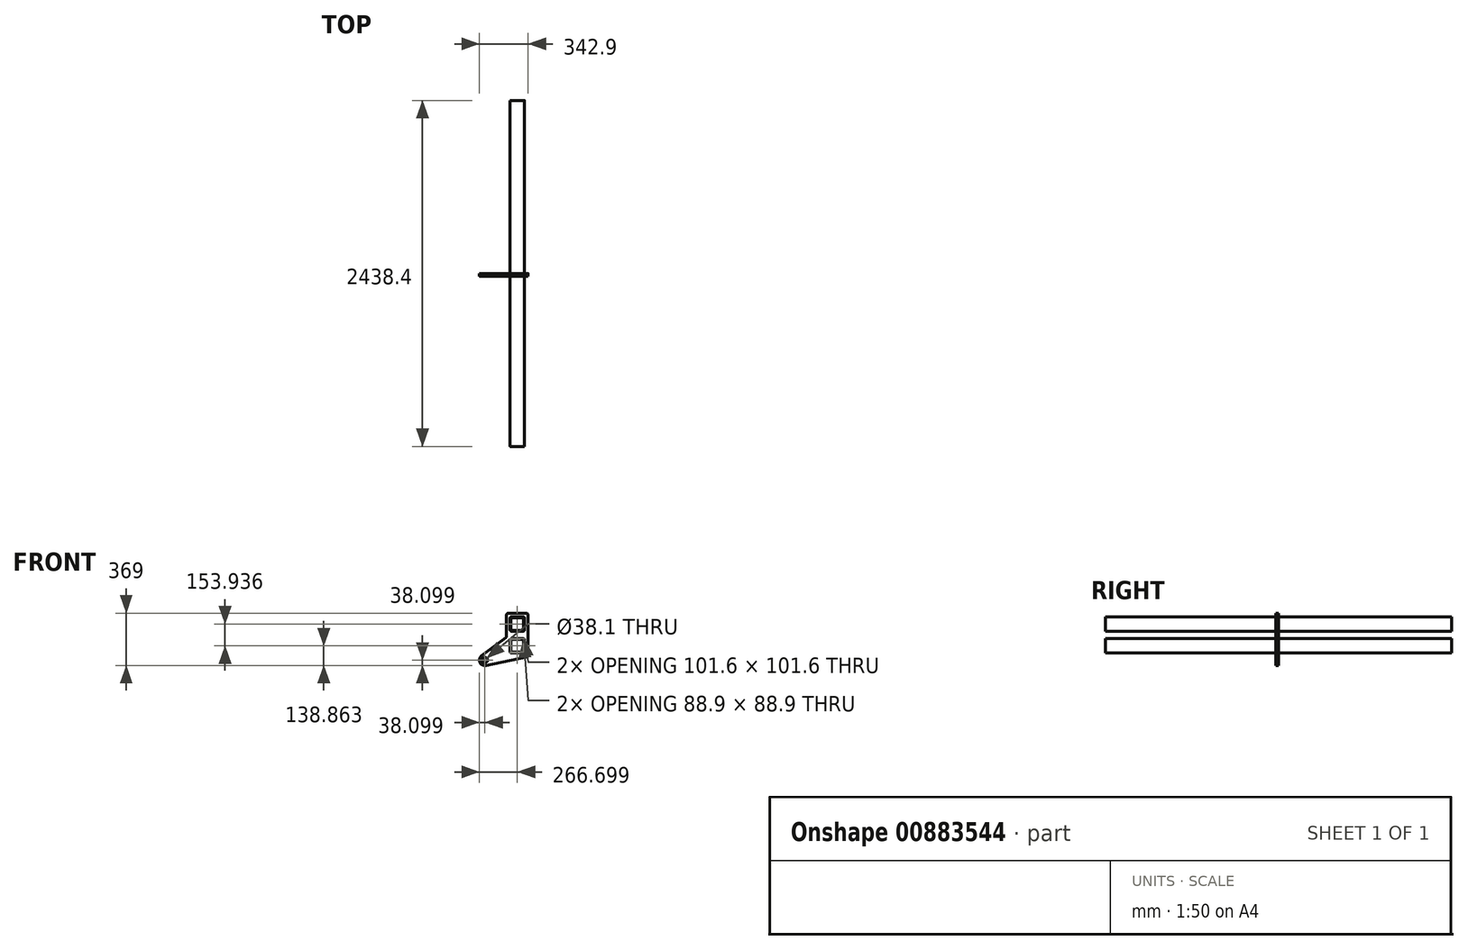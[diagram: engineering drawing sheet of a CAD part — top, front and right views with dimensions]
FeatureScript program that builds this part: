
annotation { "Feature Type Name" : "Feature", "Feature Type Description" : "" }
export const myFeature = defineFeature(function(context is Context, id is Id, definition is map)
    precondition{}
    {
        {
            var Q0;
            Q0=qCreatedBy(makeId("Front.planeOp"),FACE);
            var sketch = newSketch(context, id + "F0", { "sketchPlane" : qUnion([Q0])});
            skLineSegment(sketch, "E0.bottom", {"start": v(-15.4, 19.87) * mm, "end": v(66.9, 19.87) * mm});
            skLineSegment(sketch, "E0.top", {"start": v(-15.4, -81.73) * mm, "end": v(66.9, -81.73) * mm});
            skLineSegment(sketch, "E0.left", {"start": v(-25.05, 10.22) * mm, "end": v(-25.05, -72.07) * mm});
            skLineSegment(sketch, "E0.right", {"start": v(76.55, 10.22) * mm, "end": v(76.55, -72.07) * mm});
            skLineSegment(sketch, "E1.bottom", {"start": v(-9.05, 13.52) * mm, "end": v(60.55, 13.52) * mm});
            skLineSegment(sketch, "E1.top", {"start": v(-9.05, -75.38) * mm, "end": v(60.55, -75.38) * mm});
            skLineSegment(sketch, "E1.left", {"start": v(-18.7, 3.87) * mm, "end": v(-18.7, -65.72) * mm});
            skLineSegment(sketch, "E1.right", {"start": v(70.2, 3.87) * mm, "end": v(70.2, -65.72) * mm});
            skLineSegment(sketch, "E2.bottom", {"start": v(-15.4, 173.8) * mm, "end": v(66.9, 173.8) * mm});
            skLineSegment(sketch, "E2.top", {"start": v(-15.4, 72.2) * mm, "end": v(66.9, 72.2) * mm});
            skLineSegment(sketch, "E2.left", {"start": v(-25.05, 164.16) * mm, "end": v(-25.05, 81.86) * mm});
            skLineSegment(sketch, "E2.right", {"start": v(76.55, 164.16) * mm, "end": v(76.55, 81.86) * mm});
            skLineSegment(sketch, "E3.bottom", {"start": v(-9.05, 167.46) * mm, "end": v(60.55, 167.46) * mm});
            skLineSegment(sketch, "E3.top", {"start": v(-9.05, 78.56) * mm, "end": v(60.55, 78.56) * mm});
            skLineSegment(sketch, "E3.left", {"start": v(-18.7, 157.8) * mm, "end": v(-18.7, 88.21) * mm});
            skLineSegment(sketch, "E3.right", {"start": v(70.2, 157.8) * mm, "end": v(70.2, 88.21) * mm});
            skLineSegment(sketch, "E4.bottom", {"start": v(-37.75, 199.2) * mm, "end": v(89.25, 199.2) * mm});
            skLineSegment(sketch, "E4.left", {"start": v(-50.45, 186.5) * mm, "end": v(-50.45, 36.8) * mm});
            skLineSegment(sketch, "E4.right", {"start": v(101.95, 186.5) * mm, "end": v(101.95, -96.8) * mm});
            skArc(sketch, "E5", {"start": v(-225.74, -101.23) * mm, "mid": v(-237.56, -147.4) * mm, "end": v(-195.08, -169) * mm});
            skCircle(sketch, "E6", {"center": v(-202.85, -131.7) * mm, "radius": 19.05 * mm});
            skPoint(sketch, "E7.visualSharp", {"position": v(-18.7, 167.46) * mm});
            skArc(sketch, "E7.filletArc", {"start": v(-9.05, 167.46) * mm, "mid": v(-15.87, 164.63) * mm, "end": v(-18.7, 157.8) * mm});
            skPoint(sketch, "E8.visualSharp", {"position": v(70.2, 167.46) * mm});
            skArc(sketch, "E8.filletArc", {"start": v(70.2, 157.8) * mm, "mid": v(67.37, 164.63) * mm, "end": v(60.55, 167.46) * mm});
            skPoint(sketch, "E9.visualSharp", {"position": v(70.2, 78.56) * mm});
            skArc(sketch, "E9.filletArc", {"start": v(60.55, 78.56) * mm, "mid": v(67.37, 81.39) * mm, "end": v(70.2, 88.21) * mm});
            skPoint(sketch, "E10.visualSharp", {"position": v(-18.7, 78.56) * mm});
            skArc(sketch, "E10.filletArc", {"start": v(-18.7, 88.21) * mm, "mid": v(-15.87, 81.39) * mm, "end": v(-9.05, 78.56) * mm});
            skPoint(sketch, "E11.visualSharp", {"position": v(-25.05, 173.8) * mm});
            skArc(sketch, "E11.filletArc", {"start": v(-15.4, 173.8) * mm, "mid": v(-22.22, 170.98) * mm, "end": v(-25.05, 164.16) * mm});
            skPoint(sketch, "E12.visualSharp", {"position": v(76.55, 173.8) * mm});
            skArc(sketch, "E12.filletArc", {"start": v(76.55, 164.16) * mm, "mid": v(73.72, 170.98) * mm, "end": v(66.9, 173.8) * mm});
            skPoint(sketch, "E13.visualSharp", {"position": v(76.55, 72.2) * mm});
            skArc(sketch, "E13.filletArc", {"start": v(66.9, 72.2) * mm, "mid": v(73.72, 75.04) * mm, "end": v(76.55, 81.86) * mm});
            skPoint(sketch, "E14.visualSharp", {"position": v(-25.05, 72.2) * mm});
            skArc(sketch, "E14.filletArc", {"start": v(-25.05, 81.86) * mm, "mid": v(-22.22, 75.04) * mm, "end": v(-15.4, 72.2) * mm});
            skPoint(sketch, "E15.visualSharp", {"position": v(-25.05, 19.87) * mm});
            skArc(sketch, "E15.filletArc", {"start": v(-15.4, 19.87) * mm, "mid": v(-22.22, 17.05) * mm, "end": v(-25.05, 10.22) * mm});
            skPoint(sketch, "E16.visualSharp", {"position": v(76.55, 19.87) * mm});
            skArc(sketch, "E16.filletArc", {"start": v(76.55, 10.22) * mm, "mid": v(73.72, 17.05) * mm, "end": v(66.9, 19.87) * mm});
            skPoint(sketch, "E17.visualSharp", {"position": v(76.55, -81.73) * mm});
            skArc(sketch, "E17.filletArc", {"start": v(66.9, -81.73) * mm, "mid": v(73.72, -78.9) * mm, "end": v(76.55, -72.07) * mm});
            skPoint(sketch, "E18.visualSharp", {"position": v(-25.05, -81.73) * mm});
            skArc(sketch, "E18.filletArc", {"start": v(-25.05, -72.07) * mm, "mid": v(-22.22, -78.9) * mm, "end": v(-15.4, -81.73) * mm});
            skPoint(sketch, "E19.visualSharp", {"position": v(-18.7, -75.38) * mm});
            skArc(sketch, "E19.filletArc", {"start": v(-18.7, -65.72) * mm, "mid": v(-15.87, -72.55) * mm, "end": v(-9.05, -75.38) * mm});
            skPoint(sketch, "E20.visualSharp", {"position": v(-18.7, 13.52) * mm});
            skArc(sketch, "E20.filletArc", {"start": v(-9.05, 13.52) * mm, "mid": v(-15.87, 10.7) * mm, "end": v(-18.7, 3.87) * mm});
            skPoint(sketch, "E21.visualSharp", {"position": v(70.2, 13.52) * mm});
            skArc(sketch, "E21.filletArc", {"start": v(70.2, 3.87) * mm, "mid": v(67.37, 10.7) * mm, "end": v(60.55, 13.52) * mm});
            skPoint(sketch, "E22.visualSharp", {"position": v(70.2, -75.38) * mm});
            skArc(sketch, "E22.filletArc", {"start": v(60.55, -75.38) * mm, "mid": v(67.37, -72.55) * mm, "end": v(70.2, -65.72) * mm});
            skLineSegment(sketch, "E23", {"start": v(-225.74, -101.23) * mm, "end": v(-55.52, 26.64) * mm});
            skLineSegment(sketch, "E24", {"start": v(-195.08, -169) * mm, "end": v(91.84, -109.23) * mm});
            skPoint(sketch, "E4.top.start.orphan", {"position": v(-50.45, -107.13) * mm});
            skPoint(sketch, "E25.visualSharp", {"position": v(-50.45, 199.2) * mm});
            skArc(sketch, "E25.filletArc", {"start": v(-37.75, 199.2) * mm, "mid": v(-46.73, 195.49) * mm, "end": v(-50.45, 186.5) * mm});
            skPoint(sketch, "E26.visualSharp", {"position": v(101.95, 199.2) * mm});
            skArc(sketch, "E26.filletArc", {"start": v(101.95, 186.5) * mm, "mid": v(98.23, 195.49) * mm, "end": v(89.25, 199.2) * mm});
            skPoint(sketch, "E27.visualSharp", {"position": v(101.95, -107.13) * mm});
            skArc(sketch, "E27.filletArc", {"start": v(91.84, -109.23) * mm, "mid": v(99.1, -104.81) * mm, "end": v(101.95, -96.8) * mm});
            skPoint(sketch, "E28.visualSharp", {"position": v(-50.45, 30.45) * mm});
            skArc(sketch, "E28.filletArc", {"start": v(-55.52, 26.64) * mm, "mid": v(-51.79, 31.12) * mm, "end": v(-50.45, 36.8) * mm});
            skSolve(sketch);
        }
        {
            var Q0;
            Q0=makeQuery(id+"F0.imprint","IMPRINT",FACE,{"disambiguationData":[TD([[makeQuery(id+"F0.imprint","IMPRINT",EDGE,{"derivedFrom":sQuery(id+"F0.wireOp",EDGE,"E2.bottom")}),-1.0]])]});
            var Q1;
            Q1=makeQuery(id+"F0.imprint","IMPRINT",FACE,{"disambiguationData":[TD([[makeQuery(id+"F0.imprint","IMPRINT",EDGE,{"derivedFrom":sQuery(id+"F0.wireOp",EDGE,"E0.bottom")}),-1.0]])]});
            extrude(context, id + "F1", {"entities" : qUnion([Q0, Q1]), "endBound" : BoundingType.SYMMETRIC, "depth" : 2438.4 * mm, "offsetDistance" : 25.4 * mm});
        }
        {
            var Q0;
            Q0 = qSketchRegion(id + "F0", true);
            extrude(context, id + "F2", {"entities" : qUnion([Q0]), "depth" : 19.05 * mm, "offsetDistance" : 25.4 * mm});
        }
    });
